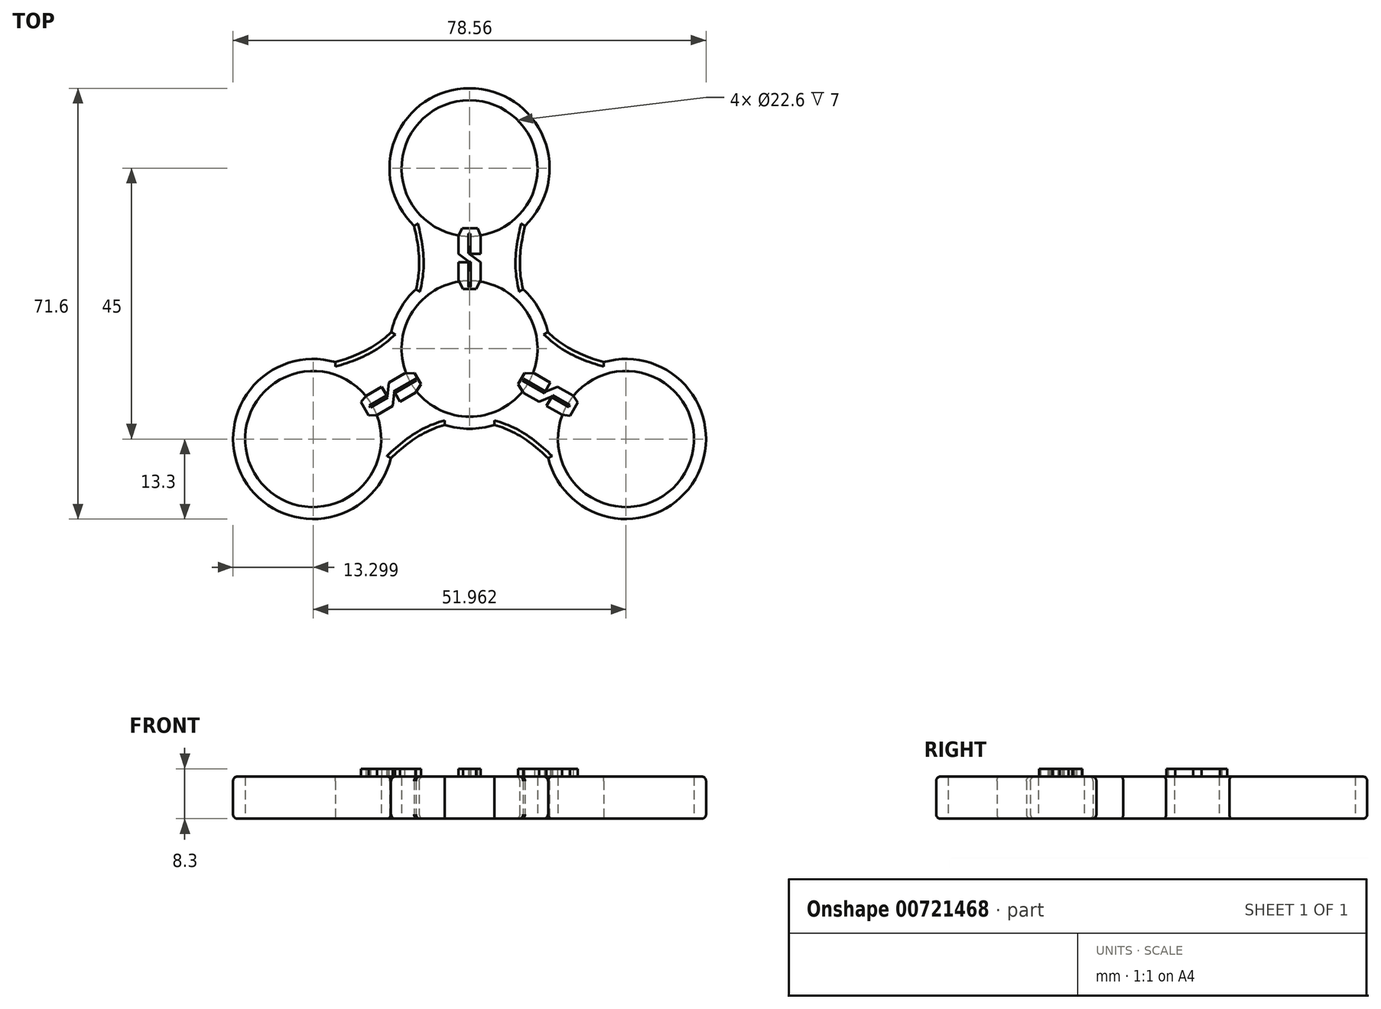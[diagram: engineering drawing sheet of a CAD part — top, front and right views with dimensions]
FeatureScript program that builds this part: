
annotation { "Feature Type Name" : "Feature", "Feature Type Description" : "" }
export const myFeature = defineFeature(function(context is Context, id is Id, definition is map)
    precondition{}
    {
        {
            var Q0;
            Q0=qCreatedBy(makeId("Top.planeOp"),FACE);
            var sketch = newSketch(context, id + "F0", { "sketchPlane" : qUnion([Q0])});
            skCircle(sketch, "E0", {"center": v(0, 0) * mm, "radius": 11.3 * mm});
            skCircle(sketch, "E1", {"center": v(0, 0) * mm, "radius": 13.3 * mm});
            skCircle(sketch, "E2", {"center": v(0, 30) * mm, "radius": 11.3 * mm});
            skCircle(sketch, "E3", {"center": v(0, 30) * mm, "radius": 13.3 * mm});
            skFitSpline(sketch, "E4.MirrorCS", {"points": [v(12.3, 30) * mm, v(8.47, 12.2) * mm, v(13.3, -5.6) * mm], "startDerivative": vector(-12, -35.77) * mm, "endDerivative": vector(1.47, -38.56) * mm});
            skLineSegment(sketch, "E5", {"start": v(-58.65, 41.17) * mm, "end": v(-58.65, 38.17) * mm});
            skLineSegment(sketch, "E6", {"start": v(-58.65, 36.77) * mm, "end": v(-58.65, 33.77) * mm});
            skLineSegment(sketch, "E7.MirrorCS", {"start": v(-54.95, 36.77) * mm, "end": v(-54.95, 33.77) * mm});
            skLineSegment(sketch, "E8.MirrorCS", {"start": v(-54.99, 41.17) * mm, "end": v(-54.99, 38.17) * mm});
            skLineSegment(sketch, "E9", {"start": v(-58.65, 41.17) * mm, "end": v(-58.03, 42.4) * mm});
            skLineSegment(sketch, "E10", {"start": v(-58.65, 33.77) * mm, "end": v(-57.87, 32.3) * mm});
            skLineSegment(sketch, "E11.MirrorCS", {"start": v(-54.95, 33.77) * mm, "end": v(-55.73, 32.3) * mm});
            skLineSegment(sketch, "E12", {"start": v(-54.99, 38.17) * mm, "end": v(-56.84, 38.17) * mm});
            skLineSegment(sketch, "E13", {"start": v(-56.84, 38.17) * mm, "end": v(-54.95, 36.77) * mm});
            skLineSegment(sketch, "E14", {"start": v(-58.65, 38.17) * mm, "end": v(-56.8, 36.77) * mm});
            skPoint(sketch, "E14.endSnap0", {"position": v(-56.8, 37.33) * mm});
            skLineSegment(sketch, "E15", {"start": v(-58.65, 36.77) * mm, "end": v(-56.8, 36.77) * mm});
            skLineSegment(sketch, "E16.bottom", {"start": v(-56.63, 36.81) * mm, "end": v(-56.97, 36.81) * mm});
            skLineSegment(sketch, "E16.top", {"start": v(-56.63, 32.61) * mm, "end": v(-56.97, 32.61) * mm});
            skLineSegment(sketch, "E16.left", {"start": v(-56.63, 36.81) * mm, "end": v(-56.63, 32.61) * mm});
            skLineSegment(sketch, "E16.right", {"start": v(-56.97, 36.81) * mm, "end": v(-56.97, 32.61) * mm});
            skPoint(sketch, "E16.middle", {"position": v(-56.8, 34.71) * mm});
            skLineSegment(sketch, "E17", {"start": v(-56.84, 38.17) * mm, "end": v(-56.84, 42.33) * mm});
            skLineSegment(sketch, "E18.bottom", {"start": v(-56.67, 41.48) * mm, "end": v(-57, 41.48) * mm});
            skLineSegment(sketch, "E18.top", {"start": v(-56.67, 38.19) * mm, "end": v(-57, 38.19) * mm});
            skLineSegment(sketch, "E18.left", {"start": v(-56.67, 41.48) * mm, "end": v(-56.67, 38.19) * mm});
            skLineSegment(sketch, "E18.right", {"start": v(-57, 41.48) * mm, "end": v(-57, 38.19) * mm});
            skPoint(sketch, "E18.middle", {"position": v(-56.84, 39.84) * mm});
            skLineSegment(sketch, "E19", {"start": v(-54.99, 41.17) * mm, "end": v(-55.47, 42.4) * mm});
            skFitSpline(sketch, "E20.MirrorCS", {"points": [v(-12.3, 30) * mm, v(-8.47, 12.2) * mm, v(-13.3, -5.6) * mm], "startDerivative": vector(12, -35.77) * mm, "endDerivative": vector(-1.47, -38.56) * mm});
            skSolve(sketch);
        }
        {
            var Q0;
            {var subQ0=sQuery(id+"F0.wireOp",EDGE,"E4.MirrorCS");var subQ1=sQuery(id+"F0.wireOp",EDGE,"E1");var subQ2=makeQuery(id+"F0.imprint","INTERSECT",VERTEX,{"disambiguationData":[OD(0.0)],"derivedFrom":[subQ1,subQ0]});Q0=makeQuery(id+"F0.imprint","IMPRINT",FACE,{"disambiguationData":[TD([[makeQuery(id+"F0.imprint","IMPRINT",EDGE,{"disambiguationData":[TD([[subQ2,-1.0]])],"derivedFrom":subQ1}),1.0]])]});}
            var Q1;
            {var subQ0=sQuery(id+"F0.wireOp",EDGE,"2f20ee7f-4028-4e4e-951a-b70d14c26677");var subQ1=sQuery(id+"F0.wireOp",EDGE,"E1");var subQ2=makeQuery(id+"F0.imprint","INTERSECT",VERTEX,{"disambiguationData":[OD(0.0)],"derivedFrom":[subQ1,subQ0]});Q1=makeQuery(id+"F0.imprint","IMPRINT",FACE,{"disambiguationData":[TD([[makeQuery(id+"F0.imprint","IMPRINT",EDGE,{"disambiguationData":[TD([[subQ2,1.0]])],"derivedFrom":subQ1}),1.0]])]});}
            var Q2;
            {var subQ0=sQuery(id+"F0.wireOp",EDGE,"2f20ee7f-4028-4e4e-951a-b70d14c26677");var subQ1=sQuery(id+"F0.wireOp",EDGE,"E3");var subQ2=makeQuery(id+"F0.imprint","INTERSECT",VERTEX,{"disambiguationData":[OD(0.0)],"derivedFrom":[subQ1,subQ0]});Q2=makeQuery(id+"F0.imprint","IMPRINT",FACE,{"disambiguationData":[TD([[makeQuery(id+"F0.imprint","IMPRINT",EDGE,{"disambiguationData":[TD([[subQ2,-1.0]])],"derivedFrom":subQ1}),1.0]])]});}
            var Q3;
            {var subQ0=sQuery(id+"F0.wireOp",EDGE,"E4.MirrorCS");var subQ1=sQuery(id+"F0.wireOp",EDGE,"E3");var subQ2=makeQuery(id+"F0.imprint","INTERSECT",VERTEX,{"disambiguationData":[OD(0.0)],"derivedFrom":[subQ1,subQ0]});Q3=makeQuery(id+"F0.imprint","IMPRINT",FACE,{"disambiguationData":[TD([[makeQuery(id+"F0.imprint","IMPRINT",EDGE,{"disambiguationData":[TD([[subQ2,1.0]])],"derivedFrom":subQ1}),1.0]])]});}
            var Q4;
            {var subQ5=sQuery(id+"F0.wireOp",EDGE,"OBWxZhdA-PvJH-oGui-LL82-nUkxGpY4iFmv");Q4=makeQuery(id+"F0.imprint","IMPRINT",FACE,{"disambiguationData":[TD([[makeQuery(id+"F0.imprint","IMPRINT",EDGE,{"derivedFrom":subQ5}),-1.0]])]});}
            var Q5;
            Q5=makeQuery(id+"F0.imprint","IMPRINT",FACE,{"disambiguationData":[TD([[makeQuery(id+"F0.imprint","IMPRINT",EDGE,{"derivedFrom":sQuery(id+"F0.wireOp",EDGE,"E0")}),-1.0]])]});
            var Q6;
            Q6=makeQuery(id+"F0.imprint","IMPRINT",FACE,{"disambiguationData":[TD([[makeQuery(id+"F0.imprint","IMPRINT",EDGE,{"derivedFrom":sQuery(id+"F0.wireOp",EDGE,"E2")}),-1.0]])]});
            var Q7;
            Q7=makeQuery(id+"F0.imprint","IMPRINT",FACE,{"disambiguationData":[TD([[makeQuery(id+"F0.imprint","IMPRINT",EDGE,{"derivedFrom":sQuery(id+"F0.wireOp",EDGE,"9b02f37e-9b39-4afa-bebc-53a3765f69b90.MirrorCS")}),1.0]])]});
            var Q8;
            {var subQ0=sQuery(id+"F0.wireOp",EDGE,"E20.MirrorCS");var subQ1=sQuery(id+"F0.wireOp",EDGE,"E1");var subQ2=makeQuery(id+"F0.imprint","INTERSECT",VERTEX,{"disambiguationData":[OD(0.0)],"derivedFrom":[subQ1,subQ0]});Q8=makeQuery(id+"F0.imprint","IMPRINT",FACE,{"disambiguationData":[TD([[makeQuery(id+"F0.imprint","IMPRINT",EDGE,{"disambiguationData":[TD([[subQ2,1.0]])],"derivedFrom":subQ1}),1.0]])]});}
            var Q9;
            {var subQ0=sQuery(id+"F0.wireOp",EDGE,"E20.MirrorCS");var subQ1=sQuery(id+"F0.wireOp",EDGE,"E1");var subQ2=makeQuery(id+"F0.imprint","INTERSECT",VERTEX,{"disambiguationData":[OD(1.0)],"derivedFrom":[subQ1,subQ0]});Q9=makeQuery(id+"F0.imprint","IMPRINT",FACE,{"disambiguationData":[TD([[makeQuery(id+"F0.imprint","IMPRINT",EDGE,{"disambiguationData":[TD([[subQ2,1.0]])],"derivedFrom":subQ1}),-1.0]])]});}
            var Q10;
            {var subQ0=sQuery(id+"F0.wireOp",EDGE,"E20.MirrorCS");var subQ1=sQuery(id+"F0.wireOp",EDGE,"E3");var subQ2=makeQuery(id+"F0.imprint","INTERSECT",VERTEX,{"disambiguationData":[OD(0.0)],"derivedFrom":[subQ1,subQ0]});Q10=makeQuery(id+"F0.imprint","IMPRINT",FACE,{"disambiguationData":[TD([[makeQuery(id+"F0.imprint","IMPRINT",EDGE,{"disambiguationData":[TD([[subQ2,-1.0]])],"derivedFrom":subQ1}),1.0]])]});}
            extrude(context, id + "F1", {"entities" : qUnion([Q0, Q1, Q2, Q3, Q4, Q5, Q6, Q7, Q8, Q9, Q10]), "depth" : 7 * mm, "offsetDistance" : 25 * mm});
        }
        {
            var Q0;
            Q0=makeQuery(id+"F1.opExtrude","SWEPT_BODY",BODY,{"disambiguationData":[OSD([sQuery(id+"F0.wireOp",EDGE,"E0"),sQuery(id+"F0.wireOp",EDGE,"E1"),sQuery(id+"F0.wireOp",EDGE,"E2"),sQuery(id+"F0.wireOp",EDGE,"E3"),sQuery(id+"F0.wireOp",EDGE,"2f20ee7f-4028-4e4e-951a-b70d14c26677"),sQuery(id+"F0.wireOp",EDGE,"E4.MirrorCS"),sQuery(id+"F0.wireOp",EDGE,"OBWxZhdA-PvJH-oGui-LL82-nUkxGpY4iFmv"),sQuery(id+"F0.wireOp",EDGE,"VyQXRtiD-QvE4-91sB-fskv-Ri9NXJNC3tFh"),sQuery(id+"F0.wireOp",EDGE,"9b02f37e-9b39-4afa-bebc-53a3765f69b90.MirrorCS"),sQuery(id+"F0.wireOp",EDGE,"b72efad4-2cd9-4a94-baac-4cae997170fb0.MirrorCS"),sQuery(id+"F0.wireOp",EDGE,"WZBJSv5I-5Trp-Ghke-d9q1-gCzl0iiRL8BR"),sQuery(id+"F0.wireOp",EDGE,"gofJsoO2-Yskn-pxnU-Y494-Dfgik08XCg3B"),sQuery(id+"F0.wireOp",EDGE,"a34870c4-c78f-46a1-99e9-9f8fcca6f6990.MirrorCS"),sQuery(id+"F0.wireOp",EDGE,"CPqXTfb4-Cb8v-TRWY-xkue-AgngyuyFBhVB"),sQuery(id+"F0.wireOp",EDGE,"runOXzn1-kFei-9hSv-rvDz-eEvDZ3INJrFD"),sQuery(id+"F0.wireOp",EDGE,"s3AkCMgg-NMMS-Ghw5-T5LG-BPR3HAijQWx7"),sQuery(id+"F0.wireOp",EDGE,"3CwPkleU-HygW-iER9-uVbC-NEvE5vYfu8BA"),sQuery(id+"F0.wireOp",EDGE,"B7rUS256-ATuu-dnwV-j8I0-nhOGhXGdm3sr.bottom"),sQuery(id+"F0.wireOp",EDGE,"B7rUS256-ATuu-dnwV-j8I0-nhOGhXGdm3sr.right"),sQuery(id+"F0.wireOp",EDGE,"nyo32sHQ-Sc8V-HGCN-re7D-FapucOhSeU9G")])]});
            var Q1;
            {var subQ0=sQuery(id+"F0.wireOp",EDGE,"2f20ee7f-4028-4e4e-951a-b70d14c26677");var subQ1=sQuery(id+"F0.wireOp",EDGE,"E1");var subQ2=makeQuery(id+"F0.imprint","INTERSECT",VERTEX,{"disambiguationData":[OD(0.0)],"derivedFrom":[subQ1,subQ0]});var subQ3=sQuery(id+"F0.wireOp",EDGE,"E4.MirrorCS");var subQ4=makeQuery(id+"F0.imprint","INTERSECT",VERTEX,{"disambiguationData":[OD(0.0)],"derivedFrom":[subQ1,subQ3]});Q1=makeQuery(id+"F1.opExtrude","SWEPT_FACE",FACE,{"disambiguationData":[OSD([subQ1]),TDD([makeQuery(id+"F0.imprint","IMPRINT",EDGE,{"disambiguationData":[TD([[subQ4,-1.0]])],"derivedFrom":subQ1}),makeQuery(id+"F0.imprint","IMPRINT",EDGE,{"disambiguationData":[TD([[subQ2,1.0]])],"derivedFrom":subQ1}),makeQuery(id+"F0.imprint","IMPRINT",EDGE,{"disambiguationData":[TD([[subQ2,-1.0]])],"derivedFrom":subQ1})])]});}
            circularPattern(context, id + "F2", {"entities" : qUnion([Q0]), "axis" : qUnion([Q1]), "angle" : 360 * degree, "instanceCount" : 3, "equalSpace" : true});
        }
        {
            var Q0;
            Q0=makeQuery(id+"F1.opExtrude","SWEPT_BODY",BODY,{"disambiguationData":[OSD([sQuery(id+"F0.wireOp",EDGE,"E0"),sQuery(id+"F0.wireOp",EDGE,"E1"),sQuery(id+"F0.wireOp",EDGE,"E2"),sQuery(id+"F0.wireOp",EDGE,"E3"),sQuery(id+"F0.wireOp",EDGE,"2f20ee7f-4028-4e4e-951a-b70d14c26677"),sQuery(id+"F0.wireOp",EDGE,"E4.MirrorCS"),sQuery(id+"F0.wireOp",EDGE,"OBWxZhdA-PvJH-oGui-LL82-nUkxGpY4iFmv"),sQuery(id+"F0.wireOp",EDGE,"VyQXRtiD-QvE4-91sB-fskv-Ri9NXJNC3tFh"),sQuery(id+"F0.wireOp",EDGE,"9b02f37e-9b39-4afa-bebc-53a3765f69b90.MirrorCS"),sQuery(id+"F0.wireOp",EDGE,"b72efad4-2cd9-4a94-baac-4cae997170fb0.MirrorCS"),sQuery(id+"F0.wireOp",EDGE,"WZBJSv5I-5Trp-Ghke-d9q1-gCzl0iiRL8BR"),sQuery(id+"F0.wireOp",EDGE,"gofJsoO2-Yskn-pxnU-Y494-Dfgik08XCg3B"),sQuery(id+"F0.wireOp",EDGE,"a34870c4-c78f-46a1-99e9-9f8fcca6f6990.MirrorCS"),sQuery(id+"F0.wireOp",EDGE,"CPqXTfb4-Cb8v-TRWY-xkue-AgngyuyFBhVB"),sQuery(id+"F0.wireOp",EDGE,"runOXzn1-kFei-9hSv-rvDz-eEvDZ3INJrFD"),sQuery(id+"F0.wireOp",EDGE,"s3AkCMgg-NMMS-Ghw5-T5LG-BPR3HAijQWx7"),sQuery(id+"F0.wireOp",EDGE,"3CwPkleU-HygW-iER9-uVbC-NEvE5vYfu8BA"),sQuery(id+"F0.wireOp",EDGE,"B7rUS256-ATuu-dnwV-j8I0-nhOGhXGdm3sr.bottom"),sQuery(id+"F0.wireOp",EDGE,"B7rUS256-ATuu-dnwV-j8I0-nhOGhXGdm3sr.right"),sQuery(id+"F0.wireOp",EDGE,"nyo32sHQ-Sc8V-HGCN-re7D-FapucOhSeU9G")])]});
            var Q1;
            Q1=makeQuery(id+"F2.opPattern","COPY",BODY,{"derivedFrom":makeQuery(id+"F1.opExtrude","SWEPT_BODY",BODY,{"disambiguationData":[OSD([sQuery(id+"F0.wireOp",EDGE,"E0"),sQuery(id+"F0.wireOp",EDGE,"E1"),sQuery(id+"F0.wireOp",EDGE,"E2"),sQuery(id+"F0.wireOp",EDGE,"E3"),sQuery(id+"F0.wireOp",EDGE,"2f20ee7f-4028-4e4e-951a-b70d14c26677"),sQuery(id+"F0.wireOp",EDGE,"E4.MirrorCS"),sQuery(id+"F0.wireOp",EDGE,"OBWxZhdA-PvJH-oGui-LL82-nUkxGpY4iFmv"),sQuery(id+"F0.wireOp",EDGE,"VyQXRtiD-QvE4-91sB-fskv-Ri9NXJNC3tFh"),sQuery(id+"F0.wireOp",EDGE,"9b02f37e-9b39-4afa-bebc-53a3765f69b90.MirrorCS"),sQuery(id+"F0.wireOp",EDGE,"b72efad4-2cd9-4a94-baac-4cae997170fb0.MirrorCS"),sQuery(id+"F0.wireOp",EDGE,"WZBJSv5I-5Trp-Ghke-d9q1-gCzl0iiRL8BR"),sQuery(id+"F0.wireOp",EDGE,"gofJsoO2-Yskn-pxnU-Y494-Dfgik08XCg3B"),sQuery(id+"F0.wireOp",EDGE,"a34870c4-c78f-46a1-99e9-9f8fcca6f6990.MirrorCS"),sQuery(id+"F0.wireOp",EDGE,"CPqXTfb4-Cb8v-TRWY-xkue-AgngyuyFBhVB"),sQuery(id+"F0.wireOp",EDGE,"runOXzn1-kFei-9hSv-rvDz-eEvDZ3INJrFD"),sQuery(id+"F0.wireOp",EDGE,"s3AkCMgg-NMMS-Ghw5-T5LG-BPR3HAijQWx7"),sQuery(id+"F0.wireOp",EDGE,"3CwPkleU-HygW-iER9-uVbC-NEvE5vYfu8BA"),sQuery(id+"F0.wireOp",EDGE,"B7rUS256-ATuu-dnwV-j8I0-nhOGhXGdm3sr.bottom"),sQuery(id+"F0.wireOp",EDGE,"B7rUS256-ATuu-dnwV-j8I0-nhOGhXGdm3sr.right"),sQuery(id+"F0.wireOp",EDGE,"nyo32sHQ-Sc8V-HGCN-re7D-FapucOhSeU9G")])]}),"instanceName":"1"});
            var Q2;
            Q2=makeQuery(id+"F2.opPattern","COPY",BODY,{"derivedFrom":makeQuery(id+"F1.opExtrude","SWEPT_BODY",BODY,{"disambiguationData":[OSD([sQuery(id+"F0.wireOp",EDGE,"E0"),sQuery(id+"F0.wireOp",EDGE,"E1"),sQuery(id+"F0.wireOp",EDGE,"E2"),sQuery(id+"F0.wireOp",EDGE,"E3"),sQuery(id+"F0.wireOp",EDGE,"2f20ee7f-4028-4e4e-951a-b70d14c26677"),sQuery(id+"F0.wireOp",EDGE,"E4.MirrorCS"),sQuery(id+"F0.wireOp",EDGE,"OBWxZhdA-PvJH-oGui-LL82-nUkxGpY4iFmv"),sQuery(id+"F0.wireOp",EDGE,"VyQXRtiD-QvE4-91sB-fskv-Ri9NXJNC3tFh"),sQuery(id+"F0.wireOp",EDGE,"9b02f37e-9b39-4afa-bebc-53a3765f69b90.MirrorCS"),sQuery(id+"F0.wireOp",EDGE,"b72efad4-2cd9-4a94-baac-4cae997170fb0.MirrorCS"),sQuery(id+"F0.wireOp",EDGE,"WZBJSv5I-5Trp-Ghke-d9q1-gCzl0iiRL8BR"),sQuery(id+"F0.wireOp",EDGE,"gofJsoO2-Yskn-pxnU-Y494-Dfgik08XCg3B"),sQuery(id+"F0.wireOp",EDGE,"a34870c4-c78f-46a1-99e9-9f8fcca6f6990.MirrorCS"),sQuery(id+"F0.wireOp",EDGE,"CPqXTfb4-Cb8v-TRWY-xkue-AgngyuyFBhVB"),sQuery(id+"F0.wireOp",EDGE,"runOXzn1-kFei-9hSv-rvDz-eEvDZ3INJrFD"),sQuery(id+"F0.wireOp",EDGE,"s3AkCMgg-NMMS-Ghw5-T5LG-BPR3HAijQWx7"),sQuery(id+"F0.wireOp",EDGE,"3CwPkleU-HygW-iER9-uVbC-NEvE5vYfu8BA"),sQuery(id+"F0.wireOp",EDGE,"B7rUS256-ATuu-dnwV-j8I0-nhOGhXGdm3sr.bottom"),sQuery(id+"F0.wireOp",EDGE,"B7rUS256-ATuu-dnwV-j8I0-nhOGhXGdm3sr.right"),sQuery(id+"F0.wireOp",EDGE,"nyo32sHQ-Sc8V-HGCN-re7D-FapucOhSeU9G")])]}),"instanceName":"2"});
            booleanBodies(context, id + "F3", {"operationType" : BooleanOperationType.UNION, "tools" : qUnion([Q0, Q1, Q2])});
        }
        {
            var Q0;
            Q0=makeQuery(id+"F2.opPattern","COPY",EDGE,{"derivedFrom":makeQuery(id+"F1.opExtrude","CAP_EDGE",EDGE,{"disambiguationData":[OSD([sQuery(id+"F0.wireOp",EDGE,"2f20ee7f-4028-4e4e-951a-b70d14c26677")])],"isStart":false}),"instanceName":"2"});
            var Q1;
            Q1=makeQuery(id+"F1.opExtrude","CAP_EDGE",EDGE,{"disambiguationData":[OSD([sQuery(id+"F0.wireOp",EDGE,"2f20ee7f-4028-4e4e-951a-b70d14c26677")])],"isStart":false});
            var Q2;
            {var subQ0=sQuery(id+"F0.wireOp",EDGE,"E4.MirrorCS");var subQ1=sQuery(id+"F0.wireOp",EDGE,"2f20ee7f-4028-4e4e-951a-b70d14c26677");var subQ2=sQuery(id+"F0.wireOp",EDGE,"E1");var subQ4=makeQuery(id+"F0.imprint","INTERSECT",VERTEX,{"disambiguationData":[OD(0.0)],"derivedFrom":[subQ2,subQ1]});var subQ5=makeQuery(id+"F0.imprint","INTERSECT",VERTEX,{"disambiguationData":[OD(0.0)],"derivedFrom":[subQ2,subQ0]});var subQ6=makeQuery(id+"F0.imprint","IMPRINT",EDGE,{"disambiguationData":[TD([[subQ4,-1.0]])],"derivedFrom":subQ2});var subQ7=makeQuery(id+"F0.imprint","IMPRINT",EDGE,{"disambiguationData":[TD([[subQ4,1.0]])],"derivedFrom":subQ2});var subQ8=makeQuery(id+"F0.imprint","IMPRINT",EDGE,{"disambiguationData":[TD([[subQ5,-1.0]])],"derivedFrom":subQ2});Q2=makeQuery(id+"F3.opBoolean","SPLIT",EDGE,{"disambiguationData":[TD([makeQuery(id+"F1.opExtrude","SWEPT_FACE",FACE,{"disambiguationData":[OSD([subQ1])]})])],"derivedFrom":makeQuery(id+"F1.opExtrude","CAP_EDGE",EDGE,{"disambiguationData":[OSD([subQ2]),TDD([subQ8,subQ7,subQ6])],"isStart":false})});}
            var Q3;
            Q3=makeQuery(id+"F1.opExtrude","CAP_EDGE",EDGE,{"disambiguationData":[OSD([sQuery(id+"F0.wireOp",EDGE,"E4.MirrorCS")])],"isStart":false});
            var Q4;
            {var subQ0=sQuery(id+"F0.wireOp",EDGE,"E4.MirrorCS");var subQ1=sQuery(id+"F0.wireOp",EDGE,"2f20ee7f-4028-4e4e-951a-b70d14c26677");var subQ2=sQuery(id+"F0.wireOp",EDGE,"E1");var subQ4=makeQuery(id+"F0.imprint","INTERSECT",VERTEX,{"disambiguationData":[OD(0.0)],"derivedFrom":[subQ2,subQ1]});var subQ5=makeQuery(id+"F0.imprint","INTERSECT",VERTEX,{"disambiguationData":[OD(0.0)],"derivedFrom":[subQ2,subQ0]});var subQ6=makeQuery(id+"F0.imprint","IMPRINT",EDGE,{"disambiguationData":[TD([[subQ4,-1.0]])],"derivedFrom":subQ2});var subQ7=makeQuery(id+"F0.imprint","IMPRINT",EDGE,{"disambiguationData":[TD([[subQ4,1.0]])],"derivedFrom":subQ2});var subQ8=makeQuery(id+"F0.imprint","IMPRINT",EDGE,{"disambiguationData":[TD([[subQ5,-1.0]])],"derivedFrom":subQ2});Q4=makeQuery(id+"F3.opBoolean","SPLIT",EDGE,{"disambiguationData":[TD([makeQuery(id+"F1.opExtrude","SWEPT_FACE",FACE,{"disambiguationData":[OSD([subQ0])]})])],"derivedFrom":makeQuery(id+"F1.opExtrude","CAP_EDGE",EDGE,{"disambiguationData":[OSD([subQ2]),TDD([subQ8,subQ7,subQ6])],"isStart":false})});}
            var Q5;
            Q5=makeQuery(id+"F2.opPattern","COPY",EDGE,{"derivedFrom":makeQuery(id+"F1.opExtrude","CAP_EDGE",EDGE,{"disambiguationData":[OSD([sQuery(id+"F0.wireOp",EDGE,"2f20ee7f-4028-4e4e-951a-b70d14c26677")])],"isStart":false}),"instanceName":"1"});
            var Q6;
            Q6=makeQuery(id+"F2.opPattern","COPY",EDGE,{"derivedFrom":makeQuery(id+"F1.opExtrude","CAP_EDGE",EDGE,{"disambiguationData":[OSD([sQuery(id+"F0.wireOp",EDGE,"E4.MirrorCS")])],"isStart":false}),"instanceName":"1"});
            var Q7;
            Q7=makeQuery(id+"F2.opPattern","COPY",EDGE,{"derivedFrom":makeQuery(id+"F1.opExtrude","CAP_EDGE",EDGE,{"disambiguationData":[OSD([sQuery(id+"F0.wireOp",EDGE,"E4.MirrorCS")])],"isStart":false}),"instanceName":"2"});
            var Q8;
            {var subQ0=sQuery(id+"F0.wireOp",EDGE,"E4.MirrorCS");var subQ1=sQuery(id+"F0.wireOp",EDGE,"2f20ee7f-4028-4e4e-951a-b70d14c26677");var subQ2=sQuery(id+"F0.wireOp",EDGE,"E1");var subQ4=makeQuery(id+"F0.imprint","INTERSECT",VERTEX,{"disambiguationData":[OD(0.0)],"derivedFrom":[subQ2,subQ1]});var subQ5=makeQuery(id+"F0.imprint","INTERSECT",VERTEX,{"disambiguationData":[OD(0.0)],"derivedFrom":[subQ2,subQ0]});var subQ6=makeQuery(id+"F0.imprint","IMPRINT",EDGE,{"disambiguationData":[TD([[subQ4,-1.0]])],"derivedFrom":subQ2});var subQ7=makeQuery(id+"F0.imprint","IMPRINT",EDGE,{"disambiguationData":[TD([[subQ4,1.0]])],"derivedFrom":subQ2});var subQ8=makeQuery(id+"F0.imprint","IMPRINT",EDGE,{"disambiguationData":[TD([[subQ5,-1.0]])],"derivedFrom":subQ2});Q8=makeQuery(id+"F3.opBoolean","SPLIT",EDGE,{"disambiguationData":[TD([makeQuery(id+"F2.opPattern","COPY",FACE,{"derivedFrom":makeQuery(id+"F1.opExtrude","SWEPT_FACE",FACE,{"disambiguationData":[OSD([subQ0])]}),"instanceName":"1"})])],"derivedFrom":makeQuery(id+"F1.opExtrude","CAP_EDGE",EDGE,{"disambiguationData":[OSD([subQ2]),TDD([subQ8,subQ7,subQ6])],"isStart":false})});}
            var Q9;
            Q9=makeQuery(id+"F2.opPattern","COPY",EDGE,{"derivedFrom":makeQuery(id+"F1.opExtrude","CAP_EDGE",EDGE,{"disambiguationData":[OSD([sQuery(id+"F0.wireOp",EDGE,"2f20ee7f-4028-4e4e-951a-b70d14c26677")])],"isStart":true}),"instanceName":"2"});
            var Q10;
            {var subQ22=sQuery(id+"F0.wireOp",EDGE,"E1");var subQ24=sQuery(id+"F0.wireOp",EDGE,"2f20ee7f-4028-4e4e-951a-b70d14c26677");var subQ25=makeQuery(id+"F0.imprint","INTERSECT",VERTEX,{"disambiguationData":[OD(0.0)],"derivedFrom":[subQ22,subQ24]});var subQ26=sQuery(id+"F0.wireOp",EDGE,"E4.MirrorCS");var subQ27=makeQuery(id+"F0.imprint","INTERSECT",VERTEX,{"disambiguationData":[OD(0.0)],"derivedFrom":[subQ22,subQ26]});var subQ28=makeQuery(id+"F0.imprint","IMPRINT",EDGE,{"disambiguationData":[TD([[subQ25,-1.0]])],"derivedFrom":subQ22});var subQ29=makeQuery(id+"F0.imprint","IMPRINT",EDGE,{"disambiguationData":[TD([[subQ25,1.0]])],"derivedFrom":subQ22});var subQ30=makeQuery(id+"F0.imprint","IMPRINT",EDGE,{"disambiguationData":[TD([[subQ27,-1.0]])],"derivedFrom":subQ22});Q10=makeQuery(id+"F3.opBoolean","SPLIT",EDGE,{"disambiguationData":[TD([makeQuery(id+"F2.opPattern","COPY",FACE,{"derivedFrom":makeQuery(id+"F1.opExtrude","SWEPT_FACE",FACE,{"disambiguationData":[OSD([subQ26])]}),"instanceName":"1"})])],"derivedFrom":makeQuery(id+"F1.opExtrude","CAP_EDGE",EDGE,{"disambiguationData":[OSD([subQ22]),TDD([subQ30,subQ29,subQ28])],"isStart":true})});}
            var Q11;
            Q11=makeQuery(id+"F2.opPattern","COPY",EDGE,{"derivedFrom":makeQuery(id+"F1.opExtrude","CAP_EDGE",EDGE,{"disambiguationData":[OSD([sQuery(id+"F0.wireOp",EDGE,"E4.MirrorCS")])],"isStart":true}),"instanceName":"1"});
            var Q12;
            Q12=makeQuery(id+"F2.opPattern","COPY",EDGE,{"derivedFrom":makeQuery(id+"F1.opExtrude","CAP_EDGE",EDGE,{"disambiguationData":[OSD([sQuery(id+"F0.wireOp",EDGE,"2f20ee7f-4028-4e4e-951a-b70d14c26677")])],"isStart":true}),"instanceName":"1"});
            var Q13;
            {var subQ21=sQuery(id+"F0.wireOp",EDGE,"E1");var subQ23=sQuery(id+"F0.wireOp",EDGE,"E4.MirrorCS");var subQ26=sQuery(id+"F0.wireOp",EDGE,"2f20ee7f-4028-4e4e-951a-b70d14c26677");var subQ29=makeQuery(id+"F0.imprint","INTERSECT",VERTEX,{"disambiguationData":[OD(0.0)],"derivedFrom":[subQ21,subQ26]});var subQ30=makeQuery(id+"F0.imprint","INTERSECT",VERTEX,{"disambiguationData":[OD(0.0)],"derivedFrom":[subQ21,subQ23]});var subQ31=makeQuery(id+"F0.imprint","IMPRINT",EDGE,{"disambiguationData":[TD([[subQ29,-1.0]])],"derivedFrom":subQ21});var subQ32=makeQuery(id+"F0.imprint","IMPRINT",EDGE,{"disambiguationData":[TD([[subQ29,1.0]])],"derivedFrom":subQ21});var subQ33=makeQuery(id+"F0.imprint","IMPRINT",EDGE,{"disambiguationData":[TD([[subQ30,-1.0]])],"derivedFrom":subQ21});Q13=makeQuery(id+"F3.opBoolean","SPLIT",EDGE,{"disambiguationData":[TD([makeQuery(id+"F1.opExtrude","SWEPT_FACE",FACE,{"disambiguationData":[OSD([subQ23])]})])],"derivedFrom":makeQuery(id+"F1.opExtrude","CAP_EDGE",EDGE,{"disambiguationData":[OSD([subQ21]),TDD([subQ33,subQ32,subQ31])],"isStart":true})});}
            var Q14;
            Q14=makeQuery(id+"F1.opExtrude","CAP_EDGE",EDGE,{"disambiguationData":[OSD([sQuery(id+"F0.wireOp",EDGE,"E4.MirrorCS")])],"isStart":true});
            var Q15;
            Q15=makeQuery(id+"F1.opExtrude","CAP_EDGE",EDGE,{"disambiguationData":[OSD([sQuery(id+"F0.wireOp",EDGE,"2f20ee7f-4028-4e4e-951a-b70d14c26677")])],"isStart":true});
            var Q16;
            {var subQ21=sQuery(id+"F0.wireOp",EDGE,"E1");var subQ23=sQuery(id+"F0.wireOp",EDGE,"2f20ee7f-4028-4e4e-951a-b70d14c26677");var subQ24=makeQuery(id+"F0.imprint","INTERSECT",VERTEX,{"disambiguationData":[OD(0.0)],"derivedFrom":[subQ21,subQ23]});var subQ25=sQuery(id+"F0.wireOp",EDGE,"E4.MirrorCS");var subQ26=makeQuery(id+"F0.imprint","INTERSECT",VERTEX,{"disambiguationData":[OD(0.0)],"derivedFrom":[subQ21,subQ25]});var subQ27=makeQuery(id+"F0.imprint","IMPRINT",EDGE,{"disambiguationData":[TD([[subQ24,-1.0]])],"derivedFrom":subQ21});var subQ28=makeQuery(id+"F0.imprint","IMPRINT",EDGE,{"disambiguationData":[TD([[subQ24,1.0]])],"derivedFrom":subQ21});var subQ29=makeQuery(id+"F0.imprint","IMPRINT",EDGE,{"disambiguationData":[TD([[subQ26,-1.0]])],"derivedFrom":subQ21});Q16=makeQuery(id+"F3.opBoolean","SPLIT",EDGE,{"disambiguationData":[TD([makeQuery(id+"F1.opExtrude","SWEPT_FACE",FACE,{"disambiguationData":[OSD([subQ23])]})])],"derivedFrom":makeQuery(id+"F1.opExtrude","CAP_EDGE",EDGE,{"disambiguationData":[OSD([subQ21]),TDD([subQ29,subQ28,subQ27])],"isStart":true})});}
            var Q17;
            Q17=makeQuery(id+"F2.opPattern","COPY",EDGE,{"derivedFrom":makeQuery(id+"F1.opExtrude","CAP_EDGE",EDGE,{"disambiguationData":[OSD([sQuery(id+"F0.wireOp",EDGE,"E4.MirrorCS")])],"isStart":true}),"instanceName":"2"});
            var Q18;
            {var subQ0=sQuery(id+"F0.wireOp",EDGE,"E4.MirrorCS");var subQ1=sQuery(id+"F0.wireOp",EDGE,"E3");var subQ2=makeQuery(id+"F0.imprint","INTERSECT",VERTEX,{"disambiguationData":[OD(0.0)],"derivedFrom":[subQ1,subQ0]});var subQ3=sQuery(id+"F0.wireOp",EDGE,"2f20ee7f-4028-4e4e-951a-b70d14c26677");var subQ4=makeQuery(id+"F0.imprint","INTERSECT",VERTEX,{"disambiguationData":[OD(0.0)],"derivedFrom":[subQ1,subQ3]});Q18=makeQuery(id+"F2.opPattern","COPY",EDGE,{"derivedFrom":makeQuery(id+"F1.opExtrude","CAP_EDGE",EDGE,{"disambiguationData":[OSD([subQ1]),TDD([makeQuery(id+"F0.imprint","IMPRINT",EDGE,{"disambiguationData":[TD([[subQ4,1.0]])],"derivedFrom":subQ1}),makeQuery(id+"F0.imprint","IMPRINT",EDGE,{"disambiguationData":[TD([[subQ4,-1.0]])],"derivedFrom":subQ1}),makeQuery(id+"F0.imprint","IMPRINT",EDGE,{"disambiguationData":[TD([[subQ2,1.0]])],"derivedFrom":subQ1})])],"isStart":true}),"instanceName":"2"});}
            var Q19;
            Q19=makeQuery(id+"F2.opPattern","COPY",EDGE,{"derivedFrom":makeQuery(id+"F1.opExtrude","CAP_EDGE",EDGE,{"disambiguationData":[OSD([sQuery(id+"F0.wireOp",EDGE,"E20.MirrorCS")])],"isStart":true}),"instanceName":"2"});
            var Q20;
            Q20=makeQuery(id+"F2.opPattern","COPY",EDGE,{"derivedFrom":makeQuery(id+"F1.opExtrude","CAP_EDGE",EDGE,{"disambiguationData":[OSD([sQuery(id+"F0.wireOp",EDGE,"E20.MirrorCS")])],"isStart":false}),"instanceName":"2"});
            var Q21;
            Q21=makeQuery(id+"F1.opExtrude","CAP_EDGE",EDGE,{"disambiguationData":[OSD([sQuery(id+"F0.wireOp",EDGE,"E20.MirrorCS")])],"isStart":false});
            var Q22;
            {var subQ0=sQuery(id+"F0.wireOp",EDGE,"E20.MirrorCS");var subQ2=sQuery(id+"F0.wireOp",EDGE,"E1");Q22=makeQuery(id+"F3.opBoolean","SPLIT",EDGE,{"disambiguationData":[TD([makeQuery(id+"F1.opExtrude","SWEPT_FACE",FACE,{"disambiguationData":[OSD([subQ0])]})])],"derivedFrom":makeQuery(id+"F1.opExtrude","CAP_EDGE",EDGE,{"disambiguationData":[OSD([subQ2])],"isStart":false})});}
            var Q23;
            Q23=makeQuery(id+"F2.opPattern","COPY",EDGE,{"derivedFrom":makeQuery(id+"F1.opExtrude","CAP_EDGE",EDGE,{"disambiguationData":[OSD([sQuery(id+"F0.wireOp",EDGE,"E3")])],"isStart":false}),"instanceName":"2"});
            var Q24;
            Q24=makeQuery(id+"F2.opPattern","COPY",EDGE,{"derivedFrom":makeQuery(id+"F1.opExtrude","CAP_EDGE",EDGE,{"disambiguationData":[OSD([sQuery(id+"F0.wireOp",EDGE,"E3")])],"isStart":false}),"instanceName":"1"});
            var Q25;
            Q25=makeQuery(id+"F2.opPattern","COPY",EDGE,{"derivedFrom":makeQuery(id+"F1.opExtrude","CAP_EDGE",EDGE,{"disambiguationData":[OSD([sQuery(id+"F0.wireOp",EDGE,"E20.MirrorCS")])],"isStart":false}),"instanceName":"1"});
            var Q26;
            Q26=makeQuery(id+"F1.opExtrude","CAP_EDGE",EDGE,{"disambiguationData":[OSD([sQuery(id+"F0.wireOp",EDGE,"E3")])],"isStart":false});
            var Q27;
            {var subQ0=sQuery(id+"F0.wireOp",EDGE,"E20.MirrorCS");var subQ2=sQuery(id+"F0.wireOp",EDGE,"E1");Q27=makeQuery(id+"F3.opBoolean","SPLIT",EDGE,{"disambiguationData":[TD([makeQuery(id+"F1.opExtrude","SWEPT_FACE",FACE,{"disambiguationData":[OSD([subQ0])]})])],"derivedFrom":makeQuery(id+"F1.opExtrude","CAP_EDGE",EDGE,{"disambiguationData":[OSD([subQ2])],"isStart":true})});}
            var Q28;
            Q28=makeQuery(id+"F1.opExtrude","CAP_EDGE",EDGE,{"disambiguationData":[OSD([sQuery(id+"F0.wireOp",EDGE,"E20.MirrorCS")])],"isStart":true});
            var Q29;
            Q29=makeQuery(id+"F1.opExtrude","CAP_EDGE",EDGE,{"disambiguationData":[OSD([sQuery(id+"F0.wireOp",EDGE,"E3")])],"isStart":true});
            var Q30;
            Q30=makeQuery(id+"F2.opPattern","COPY",EDGE,{"derivedFrom":makeQuery(id+"F1.opExtrude","CAP_EDGE",EDGE,{"disambiguationData":[OSD([sQuery(id+"F0.wireOp",EDGE,"E20.MirrorCS")])],"isStart":true}),"instanceName":"1"});
            var Q31;
            Q31=makeQuery(id+"F2.opPattern","COPY",EDGE,{"derivedFrom":makeQuery(id+"F1.opExtrude","CAP_EDGE",EDGE,{"disambiguationData":[OSD([sQuery(id+"F0.wireOp",EDGE,"E3")])],"isStart":true}),"instanceName":"1"});
            fillet(context, id + "F4", {"entities" : qUnion([Q0, Q1, Q2, Q3, Q4, Q5, Q6, Q7, Q8, Q9, Q10, Q11, Q12, Q13, Q14, Q15, Q16, Q17, Q18, Q19, Q20, Q21, Q22, Q23, Q24, Q25, Q26, Q27, Q28, Q29, Q30, Q31]), "radius" : 0.72 * mm, "tangentPropagation" : true, "allowEdgeOverflow" : false});
        }
        {
            var Q0;
            {var subQ0=makeQuery(id+"F1.opExtrude","CAP_FACE",FACE,{"disambiguationData":[OSD([sQuery(id+"F0.wireOp",EDGE,"E0"),sQuery(id+"F0.wireOp",EDGE,"E1"),sQuery(id+"F0.wireOp",EDGE,"E2"),sQuery(id+"F0.wireOp",EDGE,"E3"),sQuery(id+"F0.wireOp",EDGE,"E4.MirrorCS"),sQuery(id+"F0.wireOp",EDGE,"E20.MirrorCS")])],"isStart":false});Q0=makeQuery(id+"F3.opBoolean","MERGE",FACE,{"derivedFrom":[subQ0,makeQuery(id+"F2.opPattern","COPY",FACE,{"derivedFrom":subQ0,"instanceName":"1"}),makeQuery(id+"F2.opPattern","COPY",FACE,{"derivedFrom":subQ0,"instanceName":"2"})]});}
            var sketch = newSketch(context, id + "F5", { "sketchPlane" : qUnion([Q0])});
            skLineSegment(sketch, "E21", {"start": v(-1.85, 18.8) * mm, "end": v(-1.85, 15.8) * mm});
            skLineSegment(sketch, "E22", {"start": v(-1.85, 14.4) * mm, "end": v(-1.85, 11.4) * mm});
            skLineSegment(sketch, "E23.MirrorCS", {"start": v(1.85, 14.4) * mm, "end": v(1.85, 11.4) * mm});
            skLineSegment(sketch, "E24.MirrorCS", {"start": v(1.82, 18.8) * mm, "end": v(1.82, 15.8) * mm});
            skLineSegment(sketch, "E25", {"start": v(-1.85, 18.8) * mm, "end": v(-1.23, 20.04) * mm});
            skLineSegment(sketch, "E26", {"start": v(-1.85, 11.4) * mm, "end": v(-1.06, 9.93) * mm});
            skLineSegment(sketch, "E27.MirrorCS", {"start": v(1.85, 11.4) * mm, "end": v(1.07, 9.93) * mm});
            skLineSegment(sketch, "E28", {"start": v(1.82, 15.8) * mm, "end": v(-0.03, 15.8) * mm});
            skLineSegment(sketch, "E29", {"start": v(-0.03, 15.8) * mm, "end": v(1.85, 14.4) * mm});
            skLineSegment(sketch, "E30", {"start": v(-1.85, 15.8) * mm, "end": v(0, 14.4) * mm});
            skPoint(sketch, "E30.endSnap0", {"position": v(0, 14.97) * mm});
            skLineSegment(sketch, "E31", {"start": v(-1.85, 14.4) * mm, "end": v(0, 14.4) * mm});
            skLineSegment(sketch, "E32.bottom", {"start": v(0.17, 14.45) * mm, "end": v(-0.17, 14.45) * mm});
            skLineSegment(sketch, "E32.top", {"start": v(0.17, 10.25) * mm, "end": v(-0.17, 10.25) * mm});
            skLineSegment(sketch, "E32.left", {"start": v(0.17, 14.45) * mm, "end": v(0.17, 10.25) * mm});
            skLineSegment(sketch, "E32.right", {"start": v(-0.17, 14.45) * mm, "end": v(-0.17, 10.25) * mm});
            skPoint(sketch, "E32.middle", {"position": v(0, 12.35) * mm});
            skLineSegment(sketch, "E33", {"start": v(-0.03, 15.8) * mm, "end": v(-0.03, 19.97) * mm});
            skLineSegment(sketch, "E34.bottom", {"start": v(0.14, 19.12) * mm, "end": v(-0.2, 19.12) * mm});
            skLineSegment(sketch, "E34.top", {"start": v(0.14, 15.83) * mm, "end": v(-0.2, 15.83) * mm});
            skLineSegment(sketch, "E34.left", {"start": v(0.14, 19.12) * mm, "end": v(0.14, 15.83) * mm});
            skLineSegment(sketch, "E34.right", {"start": v(-0.2, 19.12) * mm, "end": v(-0.2, 15.83) * mm});
            skPoint(sketch, "E34.middle", {"position": v(-0.03, 17.48) * mm});
            skLineSegment(sketch, "E35", {"start": v(1.82, 18.8) * mm, "end": v(1.33, 20.05) * mm});
            skLineSegment(sketch, "E36", {"start": v(-1.06, 9.93) * mm, "end": v(1.07, 9.93) * mm});
            skLineSegment(sketch, "E37", {"start": v(-1.23, 20.04) * mm, "end": v(1.33, 20.05) * mm});
            skLineSegment(sketch, "E38.1.0", {"start": v(-11.55, -8.8) * mm, "end": v(-8.96, -7.3) * mm});
            skLineSegment(sketch, "E38.1.1", {"start": v(-8.96, -7.3) * mm, "end": v(-8.07, -5.89) * mm});
            skLineSegment(sketch, "E38.1.2", {"start": v(-8.07, -5.89) * mm, "end": v(-9.14, -4.04) * mm});
            skLineSegment(sketch, "E38.1.3", {"start": v(-10.8, -4.1) * mm, "end": v(-9.14, -4.04) * mm});
            skLineSegment(sketch, "E38.1.4", {"start": v(-13.4, -5.6) * mm, "end": v(-10.8, -4.1) * mm});
            skLineSegment(sketch, "E38.1.5", {"start": v(-12.6, -7.08) * mm, "end": v(-8.97, -4.98) * mm});
            skLineSegment(sketch, "E38.1.6", {"start": v(-12.43, -7.37) * mm, "end": v(-8.8, -5.27) * mm});
            skLineSegment(sketch, "E38.1.7", {"start": v(-8.97, -4.98) * mm, "end": v(-8.8, -5.27) * mm});
            skLineSegment(sketch, "E38.1.8", {"start": v(-11.55, -8.8) * mm, "end": v(-12.48, -7.2) * mm});
            skLineSegment(sketch, "E38.1.9", {"start": v(-12.77, -9.5) * mm, "end": v(-12.48, -7.2) * mm});
            skLineSegment(sketch, "E38.1.10", {"start": v(-15.36, -11) * mm, "end": v(-12.77, -9.5) * mm});
            skLineSegment(sketch, "E38.1.11", {"start": v(-16.46, -9.73) * mm, "end": v(-13.61, -8.09) * mm});
            skLineSegment(sketch, "E38.1.12", {"start": v(-16.63, -9.44) * mm, "end": v(-13.78, -7.8) * mm});
            skLineSegment(sketch, "E38.1.13", {"start": v(-14.6, -6.33) * mm, "end": v(-13.67, -7.93) * mm});
            skLineSegment(sketch, "E38.1.14", {"start": v(-13.67, -7.93) * mm, "end": v(-13.4, -5.6) * mm});
            skLineSegment(sketch, "E38.1.15", {"start": v(-13.78, -7.8) * mm, "end": v(-13.61, -8.09) * mm});
            skLineSegment(sketch, "E38.1.16", {"start": v(-16.63, -9.44) * mm, "end": v(-16.46, -9.73) * mm});
            skLineSegment(sketch, "E38.1.17", {"start": v(-15.36, -11) * mm, "end": v(-16.74, -11.08) * mm});
            skLineSegment(sketch, "E38.1.18", {"start": v(-16.74, -11.08) * mm, "end": v(-18.03, -8.87) * mm});
            skLineSegment(sketch, "E38.1.19", {"start": v(-17.2, -7.83) * mm, "end": v(-18.03, -8.87) * mm});
            skLineSegment(sketch, "E38.1.20", {"start": v(-17.2, -7.83) * mm, "end": v(-14.6, -6.33) * mm});
            skLineSegment(sketch, "E38.1.21", {"start": v(-12.6, -7.08) * mm, "end": v(-12.43, -7.37) * mm});
            skLineSegment(sketch, "E38.2.0", {"start": v(13.4, -5.6) * mm, "end": v(10.8, -4.1) * mm});
            skLineSegment(sketch, "E38.2.1", {"start": v(10.8, -4.1) * mm, "end": v(9.13, -4.04) * mm});
            skLineSegment(sketch, "E38.2.2", {"start": v(9.13, -4.04) * mm, "end": v(8.07, -5.9) * mm});
            skLineSegment(sketch, "E38.2.3", {"start": v(8.95, -7.3) * mm, "end": v(8.07, -5.9) * mm});
            skLineSegment(sketch, "E38.2.4", {"start": v(11.55, -8.8) * mm, "end": v(8.95, -7.3) * mm});
            skLineSegment(sketch, "E38.2.5", {"start": v(12.43, -7.38) * mm, "end": v(8.8, -5.28) * mm});
            skLineSegment(sketch, "E38.2.6", {"start": v(12.6, -7.08) * mm, "end": v(8.96, -4.98) * mm});
            skLineSegment(sketch, "E38.2.7", {"start": v(8.8, -5.28) * mm, "end": v(8.96, -4.98) * mm});
            skLineSegment(sketch, "E38.2.8", {"start": v(13.4, -5.6) * mm, "end": v(12.47, -7.2) * mm});
            skLineSegment(sketch, "E38.2.9", {"start": v(14.61, -6.3) * mm, "end": v(12.47, -7.2) * mm});
            skLineSegment(sketch, "E38.2.10", {"start": v(17.21, -7.8) * mm, "end": v(14.61, -6.3) * mm});
            skLineSegment(sketch, "E38.2.11", {"start": v(16.66, -9.39) * mm, "end": v(13.8, -7.74) * mm});
            skLineSegment(sketch, "E38.2.12", {"start": v(16.49, -9.68) * mm, "end": v(13.64, -8.04) * mm});
            skLineSegment(sketch, "E38.2.13", {"start": v(12.78, -9.48) * mm, "end": v(13.7, -7.88) * mm});
            skLineSegment(sketch, "E38.2.14", {"start": v(13.7, -7.88) * mm, "end": v(11.55, -8.8) * mm});
            skLineSegment(sketch, "E38.2.15", {"start": v(13.64, -8.04) * mm, "end": v(13.8, -7.74) * mm});
            skLineSegment(sketch, "E38.2.16", {"start": v(16.49, -9.68) * mm, "end": v(16.66, -9.39) * mm});
            skLineSegment(sketch, "E38.2.17", {"start": v(17.21, -7.8) * mm, "end": v(17.96, -8.96) * mm});
            skLineSegment(sketch, "E38.2.18", {"start": v(17.96, -8.96) * mm, "end": v(16.7, -11.18) * mm});
            skLineSegment(sketch, "E38.2.19", {"start": v(15.38, -10.98) * mm, "end": v(16.7, -11.18) * mm});
            skLineSegment(sketch, "E38.2.20", {"start": v(15.38, -10.98) * mm, "end": v(12.78, -9.48) * mm});
            skLineSegment(sketch, "E38.2.21", {"start": v(12.43, -7.38) * mm, "end": v(12.6, -7.08) * mm});
            skPoint(sketch, "E38.center", {"position": v(0, 0) * mm});
            skSolve(sketch);
        }
        {
            var Q0;
            {var subQ5=sQuery(id+"F5.wireOp",EDGE,"E22");Q0=makeQuery(id+"F5.imprint","IMPRINT",FACE,{"disambiguationData":[TD([[makeQuery(id+"F5.imprint","IMPRINT",EDGE,{"derivedFrom":subQ5}),1.0]])]});}
            var Q1;
            {var subQ7=sQuery(id+"F5.wireOp",EDGE,"E24.MirrorCS");Q1=makeQuery(id+"F5.imprint","IMPRINT",FACE,{"disambiguationData":[TD([[makeQuery(id+"F5.imprint","IMPRINT",EDGE,{"derivedFrom":subQ7}),-1.0]])]});}
            var Q2;
            {var subQ5=sQuery(id+"F5.wireOp",EDGE,"E21");Q2=makeQuery(id+"F5.imprint","IMPRINT",FACE,{"disambiguationData":[TD([[makeQuery(id+"F5.imprint","IMPRINT",EDGE,{"derivedFrom":subQ5}),1.0]])]});}
            var Q3;
            {var subQ10=sQuery(id+"F5.wireOp",EDGE,"E37");Q3=makeQuery(id+"F5.imprint","IMPRINT",FACE,{"disambiguationData":[TD([[makeQuery(id+"F5.imprint","IMPRINT",EDGE,{"derivedFrom":subQ10}),-1.0]])]});}
            var Q4;
            {var subQ1=sQuery(id+"F5.wireOp",EDGE,"E32.top");Q4=makeQuery(id+"F5.imprint","IMPRINT",FACE,{"disambiguationData":[TD([[makeQuery(id+"F5.imprint","IMPRINT",EDGE,{"derivedFrom":subQ1}),1.0]])]});}
            var Q5;
            {var subQ7=sQuery(id+"F5.wireOp",EDGE,"E38.1.4");Q5=makeQuery(id+"F5.imprint","IMPRINT",FACE,{"disambiguationData":[TD([[makeQuery(id+"F5.imprint","IMPRINT",EDGE,{"derivedFrom":subQ7}),-1.0]])]});}
            var Q6;
            {var subQ1=sQuery(id+"F5.wireOp",EDGE,"E38.1.0");Q6=makeQuery(id+"F5.imprint","IMPRINT",FACE,{"disambiguationData":[TD([[makeQuery(id+"F5.imprint","IMPRINT",EDGE,{"derivedFrom":subQ1}),1.0]])]});}
            var Q7;
            {var subQ1=sQuery(id+"F5.wireOp",EDGE,"E38.1.2");Q7=makeQuery(id+"F5.imprint","IMPRINT",FACE,{"disambiguationData":[TD([[makeQuery(id+"F5.imprint","IMPRINT",EDGE,{"derivedFrom":subQ1}),1.0]])]});}
            var Q8;
            {var subQ4=sQuery(id+"F5.wireOp",EDGE,"E38.1.16");Q8=makeQuery(id+"F5.imprint","IMPRINT",FACE,{"disambiguationData":[TD([[makeQuery(id+"F5.imprint","IMPRINT",EDGE,{"derivedFrom":subQ4}),-1.0]])]});}
            var Q9;
            {var subQ9=sQuery(id+"F5.wireOp",EDGE,"E38.2.4");Q9=makeQuery(id+"F5.imprint","IMPRINT",FACE,{"disambiguationData":[TD([[makeQuery(id+"F5.imprint","IMPRINT",EDGE,{"derivedFrom":subQ9}),-1.0]])]});}
            var Q10;
            {var subQ1=sQuery(id+"F5.wireOp",EDGE,"E38.2.0");Q10=makeQuery(id+"F5.imprint","IMPRINT",FACE,{"disambiguationData":[TD([[makeQuery(id+"F5.imprint","IMPRINT",EDGE,{"derivedFrom":subQ1}),1.0]])]});}
            var Q11;
            {var subQ4=sQuery(id+"F5.wireOp",EDGE,"E38.2.16");Q11=makeQuery(id+"F5.imprint","IMPRINT",FACE,{"disambiguationData":[TD([[makeQuery(id+"F5.imprint","IMPRINT",EDGE,{"derivedFrom":subQ4}),-1.0]])]});}
            var Q12;
            {var subQ1=sQuery(id+"F5.wireOp",EDGE,"E38.2.2");Q12=makeQuery(id+"F5.imprint","IMPRINT",FACE,{"disambiguationData":[TD([[makeQuery(id+"F5.imprint","IMPRINT",EDGE,{"derivedFrom":subQ1}),1.0]])]});}
            extrude(context, id + "F6", {"entities" : qUnion([Q0, Q1, Q2, Q3, Q4, Q5, Q6, Q7, Q8, Q9, Q10, Q11, Q12]), "operationType" : NewBodyOperationType.ADD, "depth" : 1.3 * mm, "offsetDistance" : 25 * mm});
        }
    });
